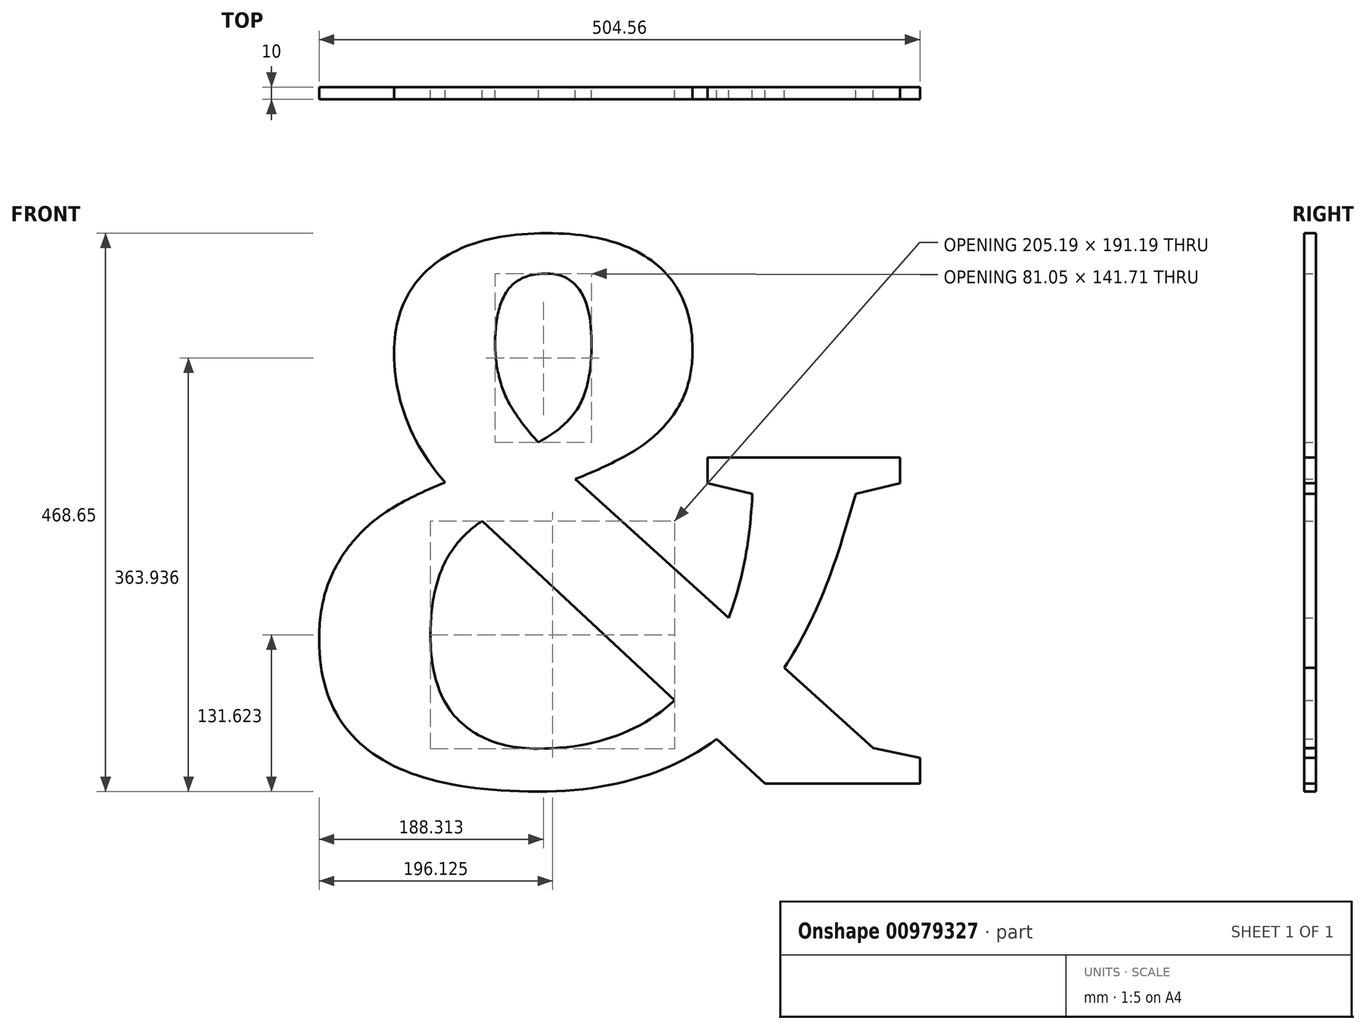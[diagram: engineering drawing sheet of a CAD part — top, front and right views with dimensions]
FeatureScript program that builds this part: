
annotation { "Feature Type Name" : "Feature", "Feature Type Description" : "" }
export const myFeature = defineFeature(function(context is Context, id is Id, definition is map)
    precondition{}
    {
        {
            var Q0;
            Q0=qCreatedBy(makeId("Front.planeOp"),FACE);
            var sketch = newSketch(context, id + "F0", { "sketchPlane" : qUnion([Q0])});
            skText(sketch, "E0", { "text": "&", "fontName": "Tinos-Bold.ttf"});
            const initialGuessF0  = {"E0": [-0.37275, -0.26198, 1, 0, 0.5]};
            skSetInitialGuess(sketch, initialGuessF0);
            skSolve(sketch);
        }
        {
            var Q0;
            Q0 = qSketchRegion(id + "F0", true);
            extrude(context, id + "F1", {"entities" : qUnion([Q0]), "depth" : 10 * mm, "offsetDistance" : 25 * mm});
        }
    });
